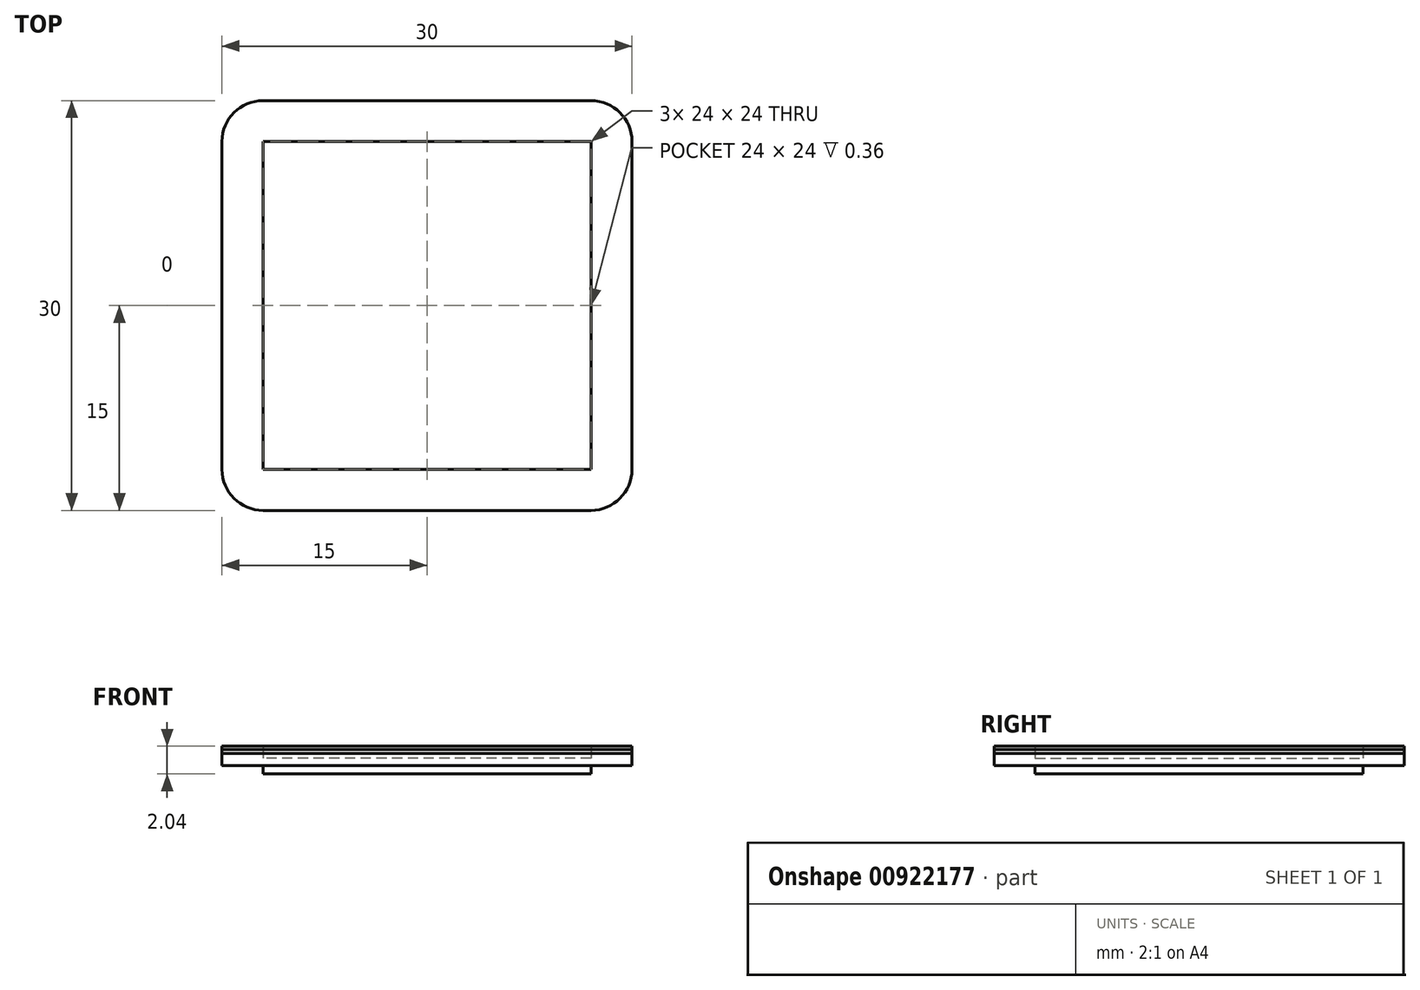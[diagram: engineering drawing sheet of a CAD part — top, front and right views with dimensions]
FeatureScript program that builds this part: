
annotation { "Feature Type Name" : "Feature", "Feature Type Description" : "" }
export const myFeature = defineFeature(function(context is Context, id is Id, definition is map)
    precondition{}
    {
        {
            var Q0;
            Q0=qCreatedBy(makeId("Top.planeOp"),FACE);
            var sketch = newSketch(context, id + "F0", { "sketchPlane" : qUnion([Q0])});
            skLineSegment(sketch, "E0.bottom", {"start": v(0, 0) * mm, "end": v(30, 0) * mm});
            skLineSegment(sketch, "E0.top", {"start": v(0, 30) * mm, "end": v(30, 30) * mm});
            skLineSegment(sketch, "E0.left", {"start": v(0, 0) * mm, "end": v(0, 30) * mm});
            skLineSegment(sketch, "E0.right", {"start": v(30, 0) * mm, "end": v(30, 30) * mm});
            skSolve(sketch);
        }
        {
            var Q0;
            Q0=makeQuery(id+"F0.imprint","IMPRINT",FACE,{"disambiguationData":[TD([[makeQuery(id+"F0.imprint","IMPRINT",EDGE,{"derivedFrom":sQuery(id+"F0.wireOp",EDGE,"E0.bottom")}),1.0]])]});
            extrude(context, id + "F1", {"entities" : qUnion([Q0]), "depth" : (.54 / 2) * mm, "offsetDistance" : 25 * mm});
        }
        {
            var Q0;
            Q0=makeQuery(id+"F1.opExtrude","SWEPT_EDGE",EDGE,{"disambiguationData":[OSD([sQuery(id+"F0.wireOp",EDGE,"E0.bottom"),sQuery(id+"F0.wireOp",EDGE,"E0.right")])]});
            var Q1;
            Q1=makeQuery(id+"F1.opExtrude","SWEPT_EDGE",EDGE,{"disambiguationData":[OSD([sQuery(id+"F0.wireOp",EDGE,"E0.top"),sQuery(id+"F0.wireOp",EDGE,"E0.right")])]});
            var Q2;
            Q2=makeQuery(id+"F1.opExtrude","SWEPT_EDGE",EDGE,{"disambiguationData":[OSD([sQuery(id+"F0.wireOp",EDGE,"E0.top"),sQuery(id+"F0.wireOp",EDGE,"E0.left")])]});
            var Q3;
            Q3=makeQuery(id+"F1.opExtrude","SWEPT_EDGE",EDGE,{"disambiguationData":[OSD([sQuery(id+"F0.wireOp",EDGE,"E0.bottom"),sQuery(id+"F0.wireOp",EDGE,"E0.left")])]});
            fillet(context, id + "F2", {"entities" : qUnion([Q0, Q1, Q2, Q3]), "radius" : 3 * mm, "tangentPropagation" : true, "allowEdgeOverflow" : false});
        }
        {
            var Q0;
            Q0=makeQuery(id+"F1.opExtrude","CAP_FACE",FACE,{"disambiguationData":[OSD([sQuery(id+"F0.wireOp",EDGE,"E0.bottom"),sQuery(id+"F0.wireOp",EDGE,"E0.top"),sQuery(id+"F0.wireOp",EDGE,"E0.left"),sQuery(id+"F0.wireOp",EDGE,"E0.right")])],"isStart":false});
            extrude(context, id + "F3", {"entities" : qUnion([Q0]), "depth" : (.54 / 2) * mm, "offsetDistance" : 25 * mm});
        }
        {
            var Q0;
            Q0=makeQuery(id+"F1.opExtrude","CAP_FACE",FACE,{"disambiguationData":[OSD([sQuery(id+"F0.wireOp",EDGE,"E0.bottom"),sQuery(id+"F0.wireOp",EDGE,"E0.top"),sQuery(id+"F0.wireOp",EDGE,"E0.left"),sQuery(id+"F0.wireOp",EDGE,"E0.right")])],"isStart":true});
            extrude(context, id + "F4", {"entities" : qUnion([Q0]), "depth" : .9 * mm, "offsetDistance" : 25 * mm});
        }
        {
            var Q0;
            Q0=makeQuery(id+"F4.opExtrude","CAP_FACE",FACE,{"disambiguationData":[OSD([sQuery(id+"F0.wireOp",EDGE,"E0.bottom"),sQuery(id+"F0.wireOp",EDGE,"E0.top"),sQuery(id+"F0.wireOp",EDGE,"E0.left"),sQuery(id+"F0.wireOp",EDGE,"E0.right")])],"isStart":false});
            var sketch = newSketch(context, id + "F5", { "sketchPlane" : qUnion([Q0])});
            skLineSegment(sketch, "E1.bottom", {"start": v(27, -3) * mm, "end": v(3, -3) * mm});
            skLineSegment(sketch, "E1.top", {"start": v(27, -27) * mm, "end": v(3, -27) * mm});
            skLineSegment(sketch, "E1.left", {"start": v(27, -3) * mm, "end": v(27, -27) * mm});
            skLineSegment(sketch, "E1.right", {"start": v(3, -3) * mm, "end": v(3, -27) * mm});
            skPoint(sketch, "E1.middle", {"position": v(15, -15) * mm});
            skPoint(sketch, "E1.middle.positionSnap0", {"position": v(15, 0) * mm});
            skPoint(sketch, "E1.middle.positionSnap1", {"position": v(0, -15) * mm});
            skPoint(sketch, "E1.centerSnap0", {"position": v(15, 0) * mm});
            skPoint(sketch, "E1.centerSnap1", {"position": v(0, -15) * mm});
            skSolve(sketch);
        }
        {
            var Q0;
            Q0=makeQuery(id+"F5.imprint","IMPRINT",FACE,{"disambiguationData":[TD([[makeQuery(id+"F5.imprint","IMPRINT",EDGE,{"derivedFrom":sQuery(id+"F5.wireOp",EDGE,"E1.bottom")}),1.0]])]});
            extrude(context, id + "F6", {"entities" : qUnion([Q0]), "operationType" : NewBodyOperationType.REMOVE, "oppositeDirection" : true, "depth" : 25 * mm, "offsetDistance" : 25 * mm});
        }
        {
            var Q0;
            Q0 = qSketchRegion(id + "F5", true);
            extrude(context, id + "F7", {"entities" : qUnion([Q0]), "depth" : .6 * mm, "offsetDistance" : 25 * mm});
        }
        {
            var Q0;
            Q0=makeQuery(id+"F5.imprint","IMPRINT",FACE,{"disambiguationData":[TD([[makeQuery(id+"F5.imprint","IMPRINT",EDGE,{"derivedFrom":sQuery(id+"F5.wireOp",EDGE,"E1.bottom")}),1.0]])]});
            extrude(context, id + "F8", {"entities" : qUnion([Q0]), "operationType" : NewBodyOperationType.ADD, "oppositeDirection" : true, "depth" : .54 * mm, "offsetDistance" : 25 * mm});
        }
    });
